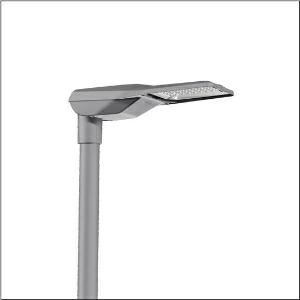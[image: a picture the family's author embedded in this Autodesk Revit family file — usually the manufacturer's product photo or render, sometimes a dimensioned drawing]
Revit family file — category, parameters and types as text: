
# Revit family: streetlight_sl_21_iq_mini___pl52_5xe2h41d08hb_c209
name_source: partatom
category: Lighting Fixtures
units: mm (PartAtom-declared; Revit-internal decimal feet)

## family parameters
Cut with Voids When Loaded = No
Host = Face
Light Source = No
Part Type = Normal
Room Calculation Point = No
Round Connector Dimension = Use Diameter
Shared = No

## types (1)
- --- (1 x LED, 9690 lm, 70.9 W, 4000K)
    Apparent Load = 71 VA
    CIE Flux Codes = 27 59 98 100 100
    Color Rendering = 70
    Color Temperature = 4000K
    Default Elevation = 1800 mm
    Description = Streetlight SL 21 iQ mini, mast luminaire, primary light control with lens, of PMMA, primary optical cover: cover, of toughened safety glass, transparent, light distribution: PL52, light emission: direct distribution, primary light characteristic: asymmetric, installation type: post-top, side-entry, LED, High Power LED, rated luminous flux: 9.690lm, luminous efficacy: 137lm/W, light colour: 740, colour temperature: 4000K, control: Auto-Match, Temp-Guard, Lumen-Switch, Night-Set, Smart-Wire, Light-Fading, Desk-Remote (wireless, voltage-free reading and setting of iQ features in the workshop via application-optimized NFC function/RFID function), optimised constant luminous flux control (CLO 2.0), presetting dimming linear, mains connection: 220..240V, AC, 50/60Hz, start of lifetime: 71W, end of service life: 75W, reduction: 31W, luminaire housing, of diecast aluminium, powder-coated, Siteco® metallic grey (DB 702S), corrosivity category C5 mid according to DIN EN ISO 12944, please order mast flange separately, inclination adjustable: 0°, 5°, 10°, 15°, sealing non-destructively replaceable, multi-level sealing system, length: 628mm, width: 235mm, height: 110mm, mast flange for spigot size: 42mm (side-entry): 5XC10008XM4, 60/48mm (side-entry/post-top): 5XC10108XM2, 76/60mm (side-entry/post-top): 5XC10108XM1, protection rating (complete): IP66, insulation class (complete): insulation class II (safety insulation), certification: CE, ENEC, ENEC+, VDE, impact resistance: IK09, permissible operating ambient temperature for outdoor applications: -40..+50°C, standard-compliant lighting for roads and squares, packaging unit: 1 piece

Light Distribution: PL52
    Height = 110 mm
    Lamp = 1 x LED
    Lamp Light Flux = 9690 lm
    Lamp Power = 70.9 W
    Lamp count = 1
    Length = 625 mm
    Luminous efficacy = 137 lm/W
    Manufacturer = Siteco
    ModVariant = No
    Model = 5XE2H41D08HB
    Number of Poles = 1
    OnlyDefault = Yes
    Power Factor = 1
    Product Name = Streetlight SL 21 iQ mini | PL52
    Product group = mast luminaire | pylon top
    ProductGroupID = 6100
    Protection Class = Protection class II
    Protection Degree = IP 66
    RLX_Detail_Level = 1
    RLX_Emergency_Light_Flux = 0 lm
    RLX_Emergency_Type = 0
    RLX_Emergency_Type_DB = No
    RlxData = <blob elided: 101873 chars, md5=fc5493a4>
    Socket = socket
    Standby Power = 0 W
    System Light Flux = 9690 lm
    System Power = 71 W
    Type Comments = factory setting: luminous flux: 100 % | dim-lin: 254 | 711 mA
    Type Image = l_1003519.jpg
    URL = http://relux.com
    VarID = @adj_108575
    Voltage = 0 V
    Weight = 0.00 kg
    Width = 234 mm

## geometry (parser evidence)
native form markers: Blend x4, Sweep x10
no freeform markers — native parametric forms only
